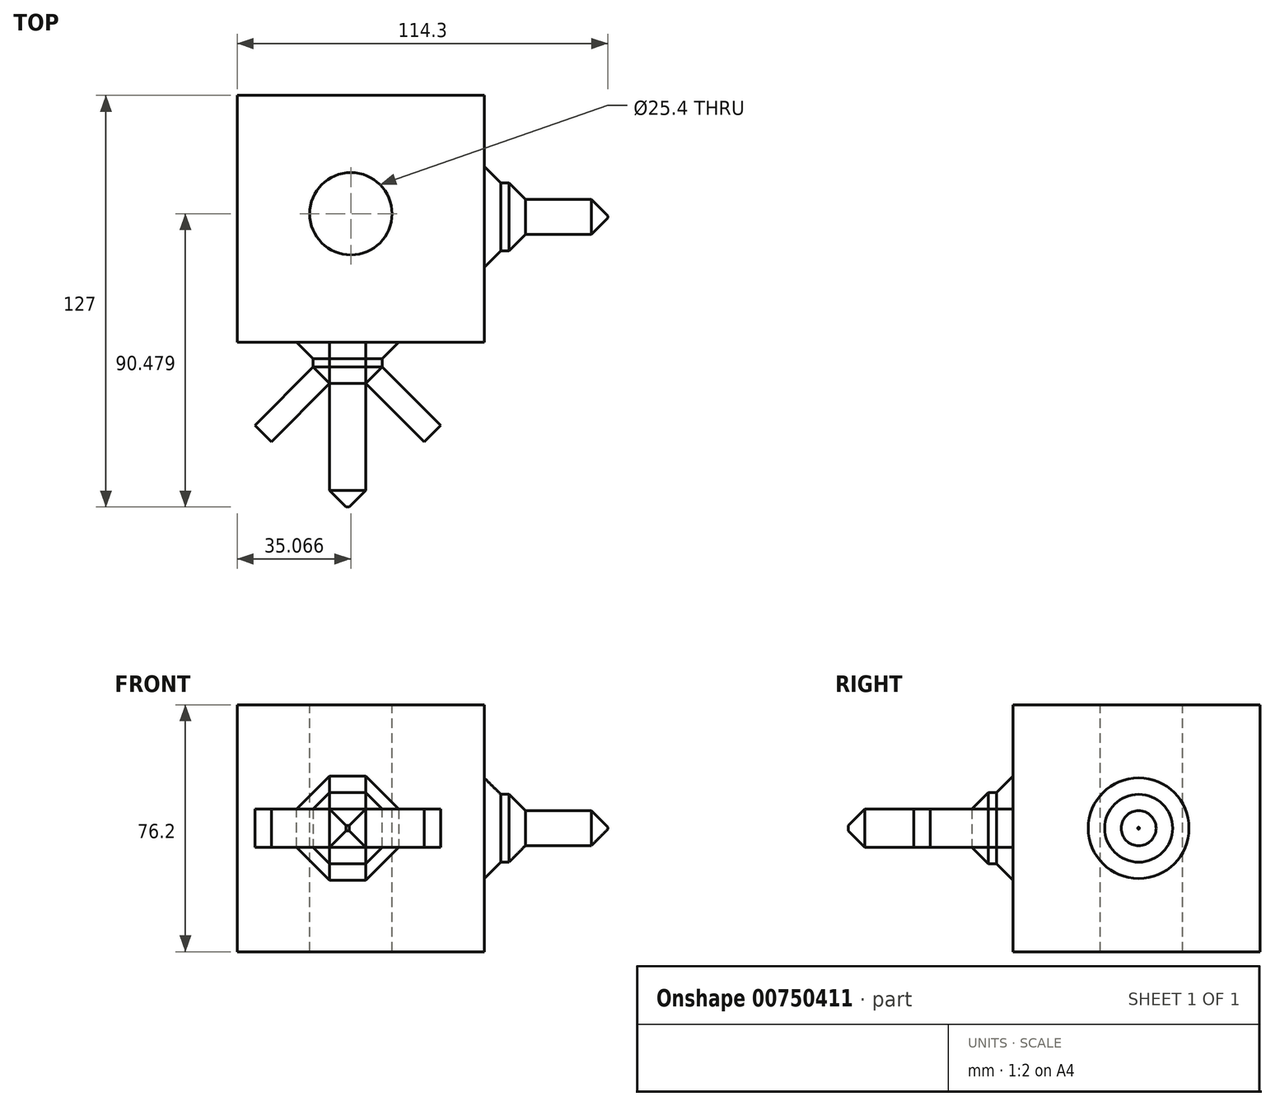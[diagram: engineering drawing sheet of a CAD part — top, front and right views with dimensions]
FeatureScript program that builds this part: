
annotation { "Feature Type Name" : "Feature", "Feature Type Description" : "" }
export const myFeature = defineFeature(function(context is Context, id is Id, definition is map)
    precondition{}
    {
        {
            var Q0;
            Q0=qCreatedBy(makeId("Front.planeOp"),FACE);
            var sketch = newSketch(context, id + "F0", { "sketchPlane" : qUnion([Q0])});
            skLineSegment(sketch, "E0.bottom", {"start": v(-103.03, -32.94) * mm, "end": v(-26.83, -32.94) * mm});
            skLineSegment(sketch, "E0.top", {"start": v(-103.03, 43.26) * mm, "end": v(-26.83, 43.26) * mm});
            skLineSegment(sketch, "E0.left", {"start": v(-103.03, -32.94) * mm, "end": v(-103.03, 43.26) * mm});
            skLineSegment(sketch, "E0.right", {"start": v(-26.83, -32.94) * mm, "end": v(-26.83, 43.26) * mm});
            skSolve(sketch);
        }
        {
            var Q0;
            Q0=makeQuery(id+"F0.imprint","IMPRINT",FACE,{"disambiguationData":[TD([[makeQuery(id+"F0.imprint","IMPRINT",EDGE,{"derivedFrom":sQuery(id+"F0.wireOp",EDGE,"E0.bottom")}),1.0]])]});
            extrude(context, id + "F1", {"entities" : qUnion([Q0]), "depth" : 76.2 * mm, "offsetDistance" : 25.4 * mm});
        }
        {
            var Q0;
            Q0=makeQuery(id+"F1.opExtrude","SWEPT_FACE",FACE,{"disambiguationData":[OSD([sQuery(id+"F0.wireOp",EDGE,"E0.top")])]});
            var sketch = newSketch(context, id + "F2", { "sketchPlane" : qUnion([Q0])});
            skPoint(sketch, "E1", {"position": v(-67.96, -36.52) * mm});
            skSolve(sketch);
        }
        {
            var Q0;
            Q0=sQuery(id+"F2.wireOp",VERTEX,"E1");
            var Q1;
            Q1=makeQuery(id+"F1.opExtrude","SWEPT_BODY",BODY,{"disambiguationData":[OSD([sQuery(id+"F0.wireOp",EDGE,"E0.bottom"),sQuery(id+"F0.wireOp",EDGE,"E0.top"),sQuery(id+"F0.wireOp",EDGE,"E0.left"),sQuery(id+"F0.wireOp",EDGE,"E0.right")])]});
            hole(context, id + "F3", {"style" : HoleStyle.SIMPLE, "endStyle" : HoleEndStyle.THROUGH, "holeDiameter" : 25.4 * mm, "majorDiameter" : 6.35 * mm, "isTappedThrough" : true, "tappedDepth" : 12.7 * mm, "tapClearance" : 3, "locations" : qUnion([Q0]), "scope" : qUnion([Q1])});
        }
        {
            var Q0;
            Q0=makeQuery(id+"F1.opExtrude","CAP_FACE",FACE,{"disambiguationData":[OSD([sQuery(id+"F0.wireOp",EDGE,"E0.bottom"),sQuery(id+"F0.wireOp",EDGE,"E0.top"),sQuery(id+"F0.wireOp",EDGE,"E0.left"),sQuery(id+"F0.wireOp",EDGE,"E0.right")])],"isStart":false});
            var sketch = newSketch(context, id + "F4", { "sketchPlane" : qUnion([Q0])});
            skPoint(sketch, "E2", {"position": v(-68.9, 5.16) * mm});
            skLineSegment(sketch, "E3.bottom", {"start": v(-58.24, 16.11) * mm, "end": v(-79.57, 16.11) * mm});
            skLineSegment(sketch, "E3.top", {"start": v(-58.24, -5.78) * mm, "end": v(-79.57, -5.78) * mm});
            skLineSegment(sketch, "E3.left", {"start": v(-58.24, 16.11) * mm, "end": v(-58.24, -5.78) * mm});
            skLineSegment(sketch, "E3.right", {"start": v(-79.57, 16.11) * mm, "end": v(-79.57, -5.78) * mm});
            skSolve(sketch);
        }
        {
            var Q0;
            Q0=makeQuery(id+"F4.imprint","IMPRINT",FACE,{"disambiguationData":[TD([[makeQuery(id+"F4.imprint","IMPRINT",EDGE,{"derivedFrom":sQuery(id+"F4.wireOp",EDGE,"E3.bottom")}),1.0]])]});
            extrude(context, id + "F5", {"entities" : qUnion([Q0]), "operationType" : NewBodyOperationType.ADD, "depth" : 12.7 * mm, "offsetDistance" : 25.4 * mm});
        }
        {
            var Q0;
            Q0=makeQuery(id+"F1.opExtrude","SWEPT_FACE",FACE,{"disambiguationData":[OSD([sQuery(id+"F0.wireOp",EDGE,"E0.right")])]});
            var sketch = newSketch(context, id + "F6", { "sketchPlane" : qUnion([Q0])});
            skPoint(sketch, "E4", {"position": v(-37.45, 5.16) * mm});
            skCircle(sketch, "E5", {"center": v(-37.45, 5.16) * mm, "radius": 10.46 * mm});
            skSolve(sketch);
        }
        {
            var Q0;
            Q0=makeQuery(id+"F6.imprint","IMPRINT",FACE,{"disambiguationData":[TD([[makeQuery(id+"F6.imprint","IMPRINT",EDGE,{"derivedFrom":sQuery(id+"F6.wireOp",EDGE,"E5")}),1.0]])]});
            extrude(context, id + "F7", {"entities" : qUnion([Q0]), "operationType" : NewBodyOperationType.ADD, "depth" : 12.7 * mm, "offsetDistance" : 25.4 * mm});
        }
        {
            var Q0;
            Q0=makeQuery(id+"F3.hole-0.boolean.opBoolean","COPY",FACE,{"derivedFrom":makeQuery(id+"F3.hole-0.opRevolve","SWEPT_FACE",FACE,{"disambiguationData":[OSD([sQuery(id+"F3.hole-0.sketch.wireOp",EDGE,"core_line_2")])]})});
            var Q1;
            Q1=makeQuery(id+"F5.opExtrude","SWEPT_FACE",FACE,{"disambiguationData":[OSD([sQuery(id+"F4.wireOp",EDGE,"E3.left")])]});
            var Q2;
            Q2=makeQuery(id+"F5.opExtrude","SWEPT_FACE",FACE,{"disambiguationData":[OSD([sQuery(id+"F4.wireOp",EDGE,"E3.bottom")])]});
            var Q3;
            Q3=makeQuery(id+"F5.opExtrude","SWEPT_FACE",FACE,{"disambiguationData":[OSD([sQuery(id+"F4.wireOp",EDGE,"E3.right")])]});
            var Q4;
            Q4=makeQuery(id+"F5.opExtrude","SWEPT_FACE",FACE,{"disambiguationData":[OSD([sQuery(id+"F4.wireOp",EDGE,"E3.top")])]});
            var Q5;
            Q5=makeQuery(id+"F7.opExtrude","CAP_FACE",FACE,{"disambiguationData":[OSD([sQuery(id+"F6.wireOp",EDGE,"E5")])],"isStart":false});
            var Q6;
            Q6=makeQuery(id+"F7.opExtrude","SWEPT_FACE",FACE,{"disambiguationData":[OSD([sQuery(id+"F6.wireOp",EDGE,"E5")])]});
            chamfer(context, id + "F8", {"entities" : qUnion([Q0, Q1, Q2, Q3, Q4, Q5, Q6]), "width" : 5.08 * mm, "tangentPropagation" : true});
        }
        {
            var Q0;
            Q0=makeQuery(id+"F7.opExtrude","CAP_FACE",FACE,{"disambiguationData":[OSD([sQuery(id+"F6.wireOp",EDGE,"E5")])],"isStart":false});
            extrude(context, id + "F9", {"entities" : qUnion([Q0]), "operationType" : NewBodyOperationType.ADD, "depth" : 12.7 * mm, "offsetDistance" : 25.4 * mm});
        }
        {
            var Q0;
            Q0=makeQuery(id+"F5.opExtrude","CAP_FACE",FACE,{"disambiguationData":[OSD([sQuery(id+"F4.wireOp",EDGE,"E3.bottom"),sQuery(id+"F4.wireOp",EDGE,"E3.top"),sQuery(id+"F4.wireOp",EDGE,"E3.left"),sQuery(id+"F4.wireOp",EDGE,"E3.right")])],"isStart":false});
            extrude(context, id + "F10", {"entities" : qUnion([Q0]), "operationType" : NewBodyOperationType.ADD, "depth" : 12.7 * mm, "offsetDistance" : 25.4 * mm});
        }
        {
            var Q0;
            {var subQ0=sQuery(id+"F4.wireOp",EDGE,"E3.right");Q0=makeQuery(id+"F8.opChamfer","BLEND_FACE",FACE,{"disambiguationData":[OSD([subQ0]),TDD([makeQuery(id+"F5.opExtrude","CAP_EDGE",EDGE,{"disambiguationData":[OSD([subQ0])],"isStart":false})])]});}
            extrude(context, id + "F11", {"entities" : qUnion([Q0]), "operationType" : NewBodyOperationType.ADD, "depth" : 25.4 * mm, "offsetDistance" : 25.4 * mm});
        }
        {
            var Q0;
            {var subQ0=sQuery(id+"F4.wireOp",EDGE,"E3.left");Q0=makeQuery(id+"F8.opChamfer","BLEND_FACE",FACE,{"disambiguationData":[OSD([subQ0]),TDD([makeQuery(id+"F5.opExtrude","CAP_EDGE",EDGE,{"disambiguationData":[OSD([subQ0])],"isStart":false})])]});}
            extrude(context, id + "F12", {"entities" : qUnion([Q0]), "operationType" : NewBodyOperationType.ADD, "depth" : 25.4 * mm, "offsetDistance" : 25.4 * mm});
        }
        {
            var Q0;
            Q0=makeQuery(id+"F10.opExtrude","CAP_FACE",FACE,{"disambiguationData":[OSD([sQuery(id+"F4.wireOp",EDGE,"E3.bottom"),sQuery(id+"F4.wireOp",EDGE,"E3.top"),sQuery(id+"F4.wireOp",EDGE,"E3.left"),sQuery(id+"F4.wireOp",EDGE,"E3.right")])],"isStart":false});
            extrude(context, id + "F13", {"entities" : qUnion([Q0]), "operationType" : NewBodyOperationType.ADD, "depth" : 25.4 * mm, "offsetDistance" : 25.4 * mm});
        }
        {
            var Q0;
            Q0=makeQuery(id+"F9.opExtrude","CAP_FACE",FACE,{"disambiguationData":[OSD([sQuery(id+"F6.wireOp",EDGE,"E5")])],"isStart":false});
            extrude(context, id + "F14", {"entities" : qUnion([Q0]), "operationType" : NewBodyOperationType.ADD, "depth" : 12.7 * mm, "offsetDistance" : 25.4 * mm});
        }
        {
            var Q0;
            Q0=makeQuery(id+"F13.opExtrude","CAP_FACE",FACE,{"disambiguationData":[OSD([sQuery(id+"F4.wireOp",EDGE,"E3.bottom"),sQuery(id+"F4.wireOp",EDGE,"E3.top"),sQuery(id+"F4.wireOp",EDGE,"E3.left"),sQuery(id+"F4.wireOp",EDGE,"E3.right")])],"isStart":false});
            var Q1;
            Q1=makeQuery(id+"F8.opChamfer","BLEND_FACE",FACE,{"disambiguationData":[OSD([sQuery(id+"F3.hole-0.sketch.wireOp",EDGE,"core_line_2"),sQuery(id+"F3.hole-0.sketch.wireOp",EDGE,"core_line_3")])]});
            var Q2;
            Q2=makeQuery(id+"F14.opExtrude","CAP_FACE",FACE,{"disambiguationData":[OSD([sQuery(id+"F6.wireOp",EDGE,"E5")])],"isStart":false});
            chamfer(context, id + "F15", {"entities" : qUnion([Q0, Q1, Q2]), "width" : 5.08 * mm, "tangentPropagation" : true});
        }
    });
